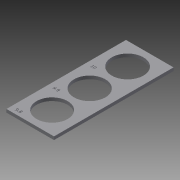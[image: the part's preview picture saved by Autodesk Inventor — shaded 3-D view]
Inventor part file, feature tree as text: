
AUTODESK INVENTOR PART (.ipt)
format: ipt  version: 2015 (Build 190159000, 159)  size: 301,056 bytes
history: native  units: in
note: dims shown in document units (in); Inventor stores cm internally (conversion verified against a paired STEP export)
features: sketch x3, extrude x3
ambient origin geometry x8: Origin, YZ Plane, XZ Plane, XY Plane, X Axis, Y Axis, Z Axis, Center Point
bodies: Solid1 (feature_tree)
feature tree (6):
  sketch  "Sketch2"  dims[d0=1.4843in d1=0.5906in]
  extrude  "Extrusion1"  Depth=0.5906in
  sketch  "Sketch4"  dims[d5=0.0394in d6=0.0in d7=0.3858in]
  extrude  "Extrusion2"  Depth=0.3858in
  extrude  "Extrusion3"  Depth=0.3937in
  sketch  "Sketch5"  dims[d8=0.2953in d9=0.2717in d10=0.3898in d11=0.2953in d12=0.4665in d13=0.3937in d14=0.2953in d15=0.4705in d16=0.0787in d17=0.0787in d18=0.0787in d19=0.0755in d20=0.0591in d21=0.0591in d22=0.0591in d23=0.3543in d24=0.3543in d25=0.3543in d27=0.0in d28=0.0787in d29=0.0in d30=0.5433in d31=0.0in d32=1.0118in d33=0.0197in d34=0.0in d35=0.0394in d36=0.0in]
